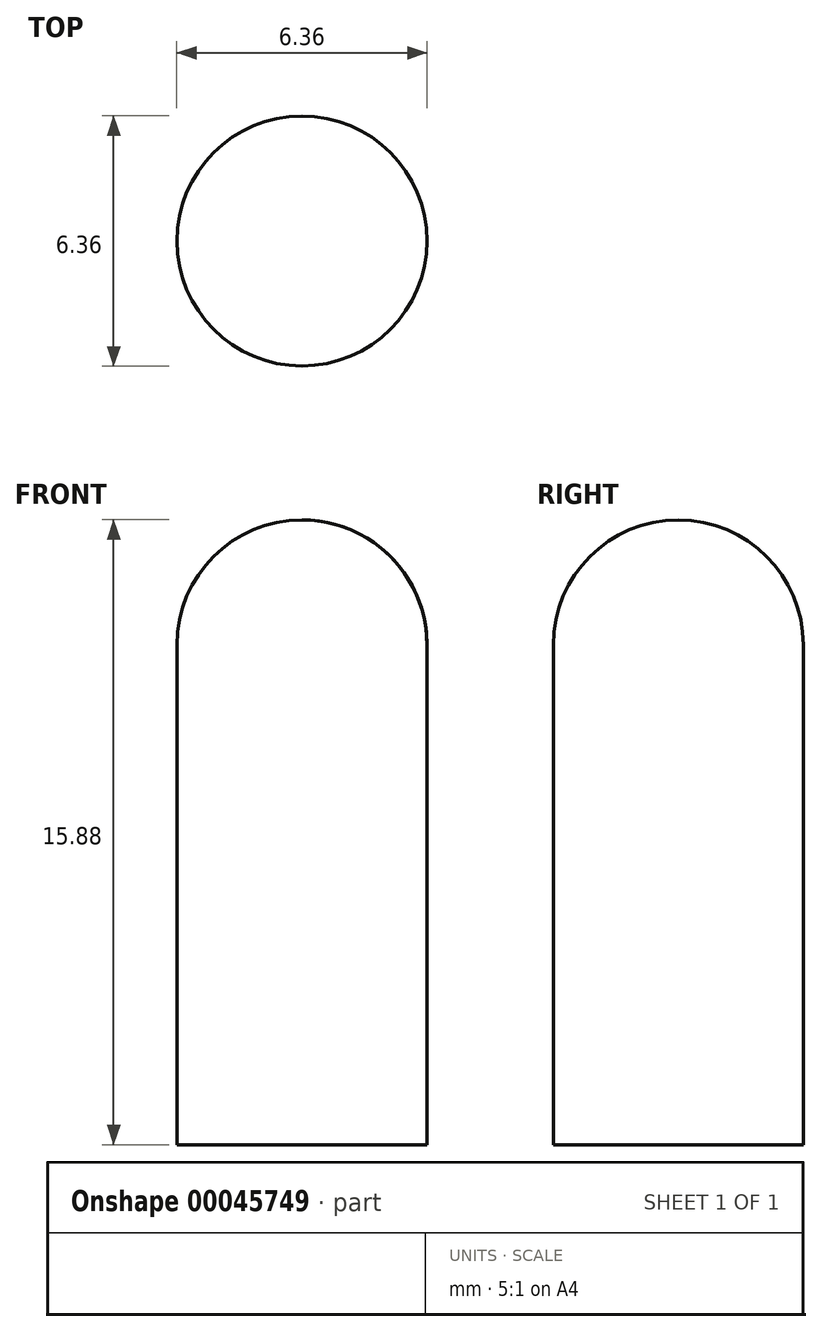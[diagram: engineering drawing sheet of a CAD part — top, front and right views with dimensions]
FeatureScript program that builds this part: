
annotation { "Feature Type Name" : "Feature", "Feature Type Description" : "" }
export const myFeature = defineFeature(function(context is Context, id is Id, definition is map)
    precondition{}
    {
        {
            var Q0;
            Q0=qCreatedBy(makeId("Front.planeOp"),FACE);
            var sketch = newSketch(context, id + "F0", { "sketchPlane" : qUnion([Q0])});
            skLineSegment(sketch, "E0", {"start": v(0, 0) * mm, "end": v(0, 15.88) * mm});
            skLineSegment(sketch, "E1", {"start": v(0, 0) * mm, "end": v(3.18, 0) * mm});
            skLineSegment(sketch, "E2", {"start": v(3.18, 0) * mm, "end": v(3.18, 12.7) * mm});
            skArc(sketch, "E3", {"start": v(3.17, 12.7) * mm, "mid": v(2.25, 14.95) * mm, "end": v(0, 15.88) * mm});
            skSolve(sketch);
        }
        {
            var Q0;
            Q0=makeQuery(id+"F0.imprint","IMPRINT",FACE,{"disambiguationData":[TD([[makeQuery(id+"F0.imprint","IMPRINT",EDGE,{"derivedFrom":sQuery(id+"F0.wireOp",EDGE,"E0")}),-1.0]])]});
            var Q1;
            Q1=sQuery(id+"F0.wireOp",EDGE,"E0");
            revolve(context, id + "F1", {"entities" : qUnion([Q0]), "axis" : qUnion([Q1]), "revolveType" : RevolveType.FULL});
        }
    });
